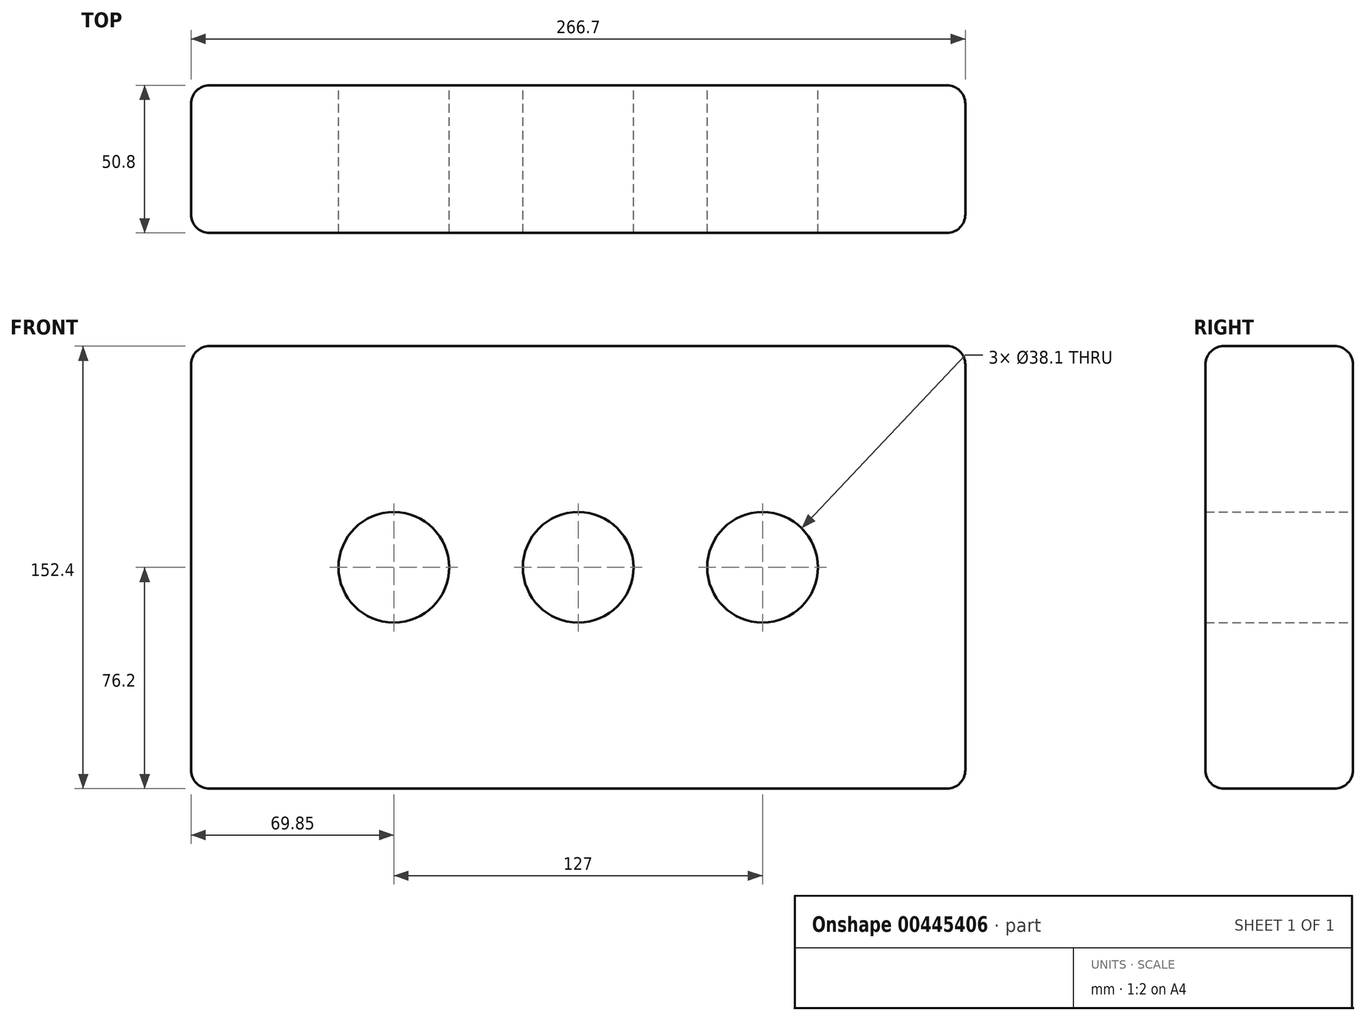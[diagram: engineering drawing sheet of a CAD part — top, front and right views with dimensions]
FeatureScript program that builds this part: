
annotation { "Feature Type Name" : "Feature", "Feature Type Description" : "" }
export const myFeature = defineFeature(function(context is Context, id is Id, definition is map)
    precondition{}
    {
        {
            var Q0;
            Q0=qCreatedBy(makeId("Front.planeOp"),FACE);
            var sketch = newSketch(context, id + "F0", { "sketchPlane" : qUnion([Q0])});
            skLineSegment(sketch, "E0.bottom", {"start": v(-133.35, 76.2) * mm, "end": v(133.35, 76.2) * mm});
            skLineSegment(sketch, "E0.top", {"start": v(-133.35, -76.2) * mm, "end": v(133.35, -76.2) * mm});
            skLineSegment(sketch, "E0.left", {"start": v(-133.35, 76.2) * mm, "end": v(-133.35, -76.2) * mm});
            skLineSegment(sketch, "E0.right", {"start": v(133.35, 76.2) * mm, "end": v(133.35, -76.2) * mm});
            skPoint(sketch, "E0.middle", {"position": v(0, 0) * mm});
            skSolve(sketch);
        }
        {
            var Q0;
            Q0=makeQuery(id+"F0.imprint","IMPRINT",FACE,{"disambiguationData":[TD([[makeQuery(id+"F0.imprint","IMPRINT",EDGE,{"derivedFrom":sQuery(id+"F0.wireOp",EDGE,"E0.bottom")}),-1.0]])]});
            extrude(context, id + "F1", {"entities" : qUnion([Q0]), "depth" : 50.8 * mm});
        }
        {
            var Q0;
            Q0=makeQuery(id+"F1.opExtrude","CAP_EDGE",EDGE,{"disambiguationData":[OSD([sQuery(id+"F0.wireOp",EDGE,"E0.bottom")])],"isStart":false});
            var Q1;
            Q1=makeQuery(id+"F1.opExtrude","SWEPT_FACE",FACE,{"disambiguationData":[OSD([sQuery(id+"F0.wireOp",EDGE,"E0.bottom")])]});
            var Q2;
            Q2=makeQuery(id+"F1.opExtrude","CAP_EDGE",EDGE,{"disambiguationData":[OSD([sQuery(id+"F0.wireOp",EDGE,"E0.top")])],"isStart":false});
            var Q3;
            Q3=makeQuery(id+"F1.opExtrude","SWEPT_FACE",FACE,{"disambiguationData":[OSD([sQuery(id+"F0.wireOp",EDGE,"E0.top")])]});
            var Q4;
            Q4=makeQuery(id+"F1.opExtrude","CAP_EDGE",EDGE,{"disambiguationData":[OSD([sQuery(id+"F0.wireOp",EDGE,"E0.left")])],"isStart":false});
            var Q5;
            Q5=makeQuery(id+"F1.opExtrude","CAP_EDGE",EDGE,{"disambiguationData":[OSD([sQuery(id+"F0.wireOp",EDGE,"E0.left")])],"isStart":true});
            var Q6;
            Q6=makeQuery(id+"F1.opExtrude","CAP_EDGE",EDGE,{"disambiguationData":[OSD([sQuery(id+"F0.wireOp",EDGE,"E0.right")])],"isStart":false});
            var Q7;
            Q7=makeQuery(id+"F1.opExtrude","CAP_EDGE",EDGE,{"disambiguationData":[OSD([sQuery(id+"F0.wireOp",EDGE,"E0.right")])],"isStart":true});
            fillet(context, id + "F2", {"entities" : qUnion([Q0, Q1, Q2, Q3, Q4, Q5, Q6, Q7]), "radius" : 6.35 * mm, "tangentPropagation" : true, "allowEdgeOverflow" : false});
        }
        {
            var Q0;
            Q0=makeQuery(id+"F1.opExtrude","CAP_FACE",FACE,{"disambiguationData":[OSD([sQuery(id+"F0.wireOp",EDGE,"E0.bottom"),sQuery(id+"F0.wireOp",EDGE,"E0.top"),sQuery(id+"F0.wireOp",EDGE,"E0.left"),sQuery(id+"F0.wireOp",EDGE,"E0.right")])],"isStart":true});
            var sketch = newSketch(context, id + "F3", { "sketchPlane" : qUnion([Q0])});
            skCircle(sketch, "E1", {"center": v(0, 0) * mm, "radius": 19.05 * mm});
            skLineSegment(sketch, "E2", {"start": v(0, 0) * mm, "end": v(-63.5, 0) * mm});
            skCircle(sketch, "E3", {"center": v(-63.5, 0) * mm, "radius": 19.05 * mm});
            skLineSegment(sketch, "E4", {"start": v(0, 0) * mm, "end": v(63.5, 0) * mm});
            skCircle(sketch, "E5", {"center": v(63.5, 0) * mm, "radius": 19.05 * mm});
            skSolve(sketch);
        }
        {
            var Q0;
            Q0=makeQuery(id+"F3.imprint","IMPRINT",FACE,{"disambiguationData":[TD([[makeQuery(id+"F3.imprint","IMPRINT",EDGE,{"derivedFrom":sQuery(id+"F3.wireOp",EDGE,"E3")}),1.0]])]});
            var Q1;
            {var subQ0=sQuery(id+"F3.wireOp",EDGE,"E2");var subQ1=sQuery(id+"F3.wireOp",EDGE,"E1");var subQ2=makeQuery(id+"F3.imprint","INTERSECT",VERTEX,{"derivedFrom":[subQ1,subQ0]});Q1=makeQuery(id+"F3.imprint","IMPRINT",FACE,{"disambiguationData":[TD([[makeQuery(id+"F3.imprint","IMPRINT",EDGE,{"disambiguationData":[TD([[subQ2,1.0]])],"derivedFrom":subQ1}),1.0]])]});}
            var Q2;
            {var subQ0=sQuery(id+"F3.wireOp",EDGE,"E2");var subQ1=sQuery(id+"F3.wireOp",EDGE,"E1");var subQ2=makeQuery(id+"F3.imprint","INTERSECT",VERTEX,{"derivedFrom":[subQ1,subQ0]});Q2=makeQuery(id+"F3.imprint","IMPRINT",FACE,{"disambiguationData":[TD([[makeQuery(id+"F3.imprint","IMPRINT",EDGE,{"disambiguationData":[TD([[subQ2,-1.0]])],"derivedFrom":subQ1}),1.0]])]});}
            var Q3;
            Q3=makeQuery(id+"F3.imprint","IMPRINT",FACE,{"disambiguationData":[TD([[makeQuery(id+"F3.imprint","IMPRINT",EDGE,{"derivedFrom":sQuery(id+"F3.wireOp",EDGE,"E5")}),1.0]])]});
            extrude(context, id + "F4", {"entities" : qUnion([Q0, Q1, Q2, Q3]), "operationType" : NewBodyOperationType.REMOVE, "oppositeDirection" : true, "depth" : 63.5 * mm});
        }
    });
